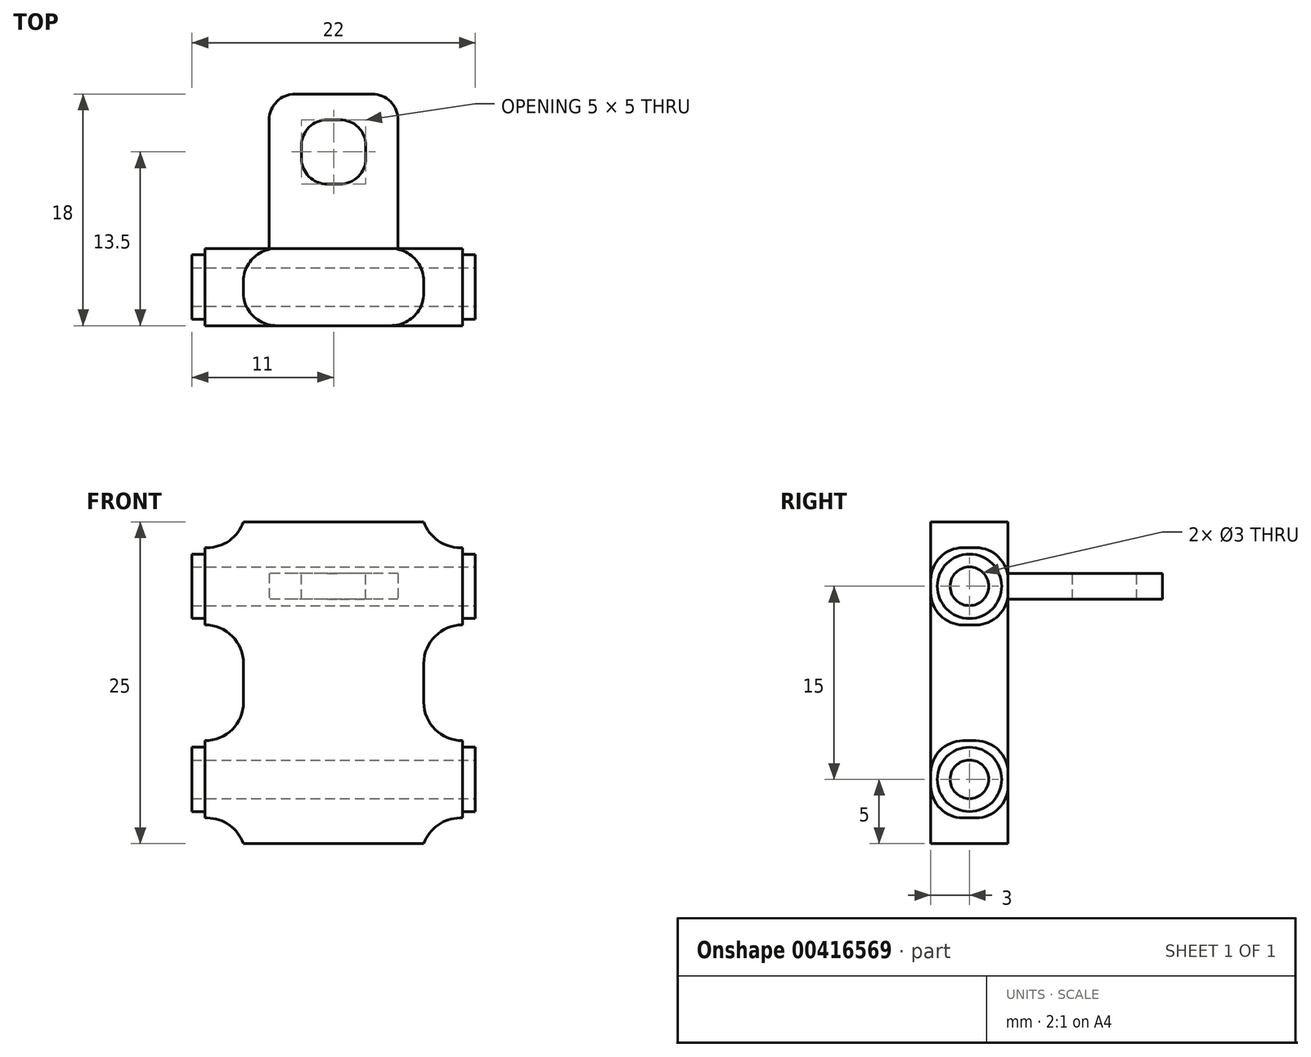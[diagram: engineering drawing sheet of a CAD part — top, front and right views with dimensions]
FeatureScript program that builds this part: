
annotation { "Feature Type Name" : "Feature", "Feature Type Description" : "" }
export const myFeature = defineFeature(function(context is Context, id is Id, definition is map)
    precondition{}
    {
        {
            var Q0;
            Q0=qCreatedBy(makeId("Top.planeOp"),FACE);
            var sketch = newSketch(context, id + "F0", { "sketchPlane" : qUnion([Q0])});
            skLineSegment(sketch, "E0.bottom", {"start": v(-10, 3) * mm, "end": v(10, 3) * mm});
            skLineSegment(sketch, "E0.top", {"start": v(-10, -3) * mm, "end": v(10, -3) * mm});
            skLineSegment(sketch, "E0.left", {"start": v(-10, 3) * mm, "end": v(-10, -3) * mm});
            skLineSegment(sketch, "E0.right", {"start": v(10, 3) * mm, "end": v(10, -3) * mm});
            skSolve(sketch);
        }
        {
            var Q0;
            Q0=makeQuery(id+"F0.imprint","IMPRINT",FACE,{"disambiguationData":[TD([[makeQuery(id+"F0.imprint","IMPRINT",EDGE,{"derivedFrom":sQuery(id+"F0.wireOp",EDGE,"fq8zQIuJ-jQ8N-2xgu-dbAs-BcYjrlKz9kw7")}),-1.0]])]});
            var Q1;
            Q1=makeQuery(id+"F0.imprint","IMPRINT",FACE,{"disambiguationData":[TD([[makeQuery(id+"F0.imprint","IMPRINT",EDGE,{"derivedFrom":sQuery(id+"F0.wireOp",EDGE,"E0.bottom")}),-1.0]])]});
            extrude(context, id + "F1", {"entities" : qUnion([Q0, Q1]), "depth" : 25 * mm});
        }
        {
            var Q0;
            Q0=makeQuery(id+"F1.opExtrude","SWEPT_FACE",FACE,{"disambiguationData":[OSD([sQuery(id+"F0.wireOp",EDGE,"E0.right")])]});
            var sketch = newSketch(context, id + "F2", { "sketchPlane" : qUnion([Q0])});
            skCircle(sketch, "E1", {"center": v(0, 20) * mm, "radius": 1.5 * mm});
            skCircle(sketch, "E2", {"center": v(0, 5) * mm, "radius": 1.5 * mm});
            skCircle(sketch, "E3", {"center": v(0, 20) * mm, "radius": 2.5 * mm});
            skCircle(sketch, "E4", {"center": v(0, 5) * mm, "radius": 2.5 * mm});
            skSolve(sketch);
        }
        {
            var Q0;
            Q0=makeQuery(id+"F2.imprint","IMPRINT",FACE,{"disambiguationData":[TD([[makeQuery(id+"F2.imprint","IMPRINT",EDGE,{"derivedFrom":sQuery(id+"F2.wireOp",EDGE,"E1")}),1.0]])]});
            var Q1;
            Q1=makeQuery(id+"F2.imprint","IMPRINT",FACE,{"disambiguationData":[TD([[makeQuery(id+"F2.imprint","IMPRINT",EDGE,{"derivedFrom":sQuery(id+"F2.wireOp",EDGE,"E2")}),1.0]])]});
            extrude(context, id + "F3", {"entities" : qUnion([Q0, Q1]), "operationType" : NewBodyOperationType.REMOVE, "oppositeDirection" : true, "depth" : 25 * mm});
        }
        {
            var Q0;
            Q0=makeQuery(id+"F1.opExtrude","SWEPT_FACE",FACE,{"disambiguationData":[OSD([sQuery(id+"F0.wireOp",EDGE,"E0.top")])]});
            var sketch = newSketch(context, id + "F4", { "sketchPlane" : qUnion([Q0])});
            skLineSegment(sketch, "E5.bottom", {"start": v(-10, 0) * mm, "end": v(-7, 0) * mm});
            skLineSegment(sketch, "E5.top", {"start": v(-10, 2) * mm, "end": v(-7, 2) * mm});
            skLineSegment(sketch, "E5.left", {"start": v(-10, 0) * mm, "end": v(-10, 2) * mm});
            skLineSegment(sketch, "E5.right", {"start": v(-7, 0) * mm, "end": v(-7, 2) * mm});
            skLineSegment(sketch, "E6.bottom", {"start": v(-10, 25) * mm, "end": v(-7, 25) * mm});
            skLineSegment(sketch, "E6.top", {"start": v(-10, 23) * mm, "end": v(-7, 23) * mm});
            skLineSegment(sketch, "E6.left", {"start": v(-10, 25) * mm, "end": v(-10, 23) * mm});
            skLineSegment(sketch, "E6.right", {"start": v(-7, 25) * mm, "end": v(-7, 23) * mm});
            skLineSegment(sketch, "E7.bottom", {"start": v(-10, 17) * mm, "end": v(-7, 17) * mm});
            skLineSegment(sketch, "E7.top", {"start": v(-10, 8) * mm, "end": v(-7, 8) * mm});
            skLineSegment(sketch, "E7.left", {"start": v(-10, 17) * mm, "end": v(-10, 8) * mm});
            skLineSegment(sketch, "E7.right", {"start": v(-7, 17) * mm, "end": v(-7, 8) * mm});
            skLineSegment(sketch, "E8.bottom", {"start": v(10, 25) * mm, "end": v(7, 25) * mm});
            skLineSegment(sketch, "E8.top", {"start": v(10, 23) * mm, "end": v(7, 23) * mm});
            skLineSegment(sketch, "E8.left", {"start": v(10, 25) * mm, "end": v(10, 23) * mm});
            skLineSegment(sketch, "E8.right", {"start": v(7, 25) * mm, "end": v(7, 23) * mm});
            skLineSegment(sketch, "E9.bottom", {"start": v(10, 0) * mm, "end": v(7, 0) * mm});
            skLineSegment(sketch, "E9.top", {"start": v(10, 2) * mm, "end": v(7, 2) * mm});
            skLineSegment(sketch, "E9.left", {"start": v(10, 0) * mm, "end": v(10, 2) * mm});
            skLineSegment(sketch, "E9.right", {"start": v(7, 0) * mm, "end": v(7, 2) * mm});
            skLineSegment(sketch, "E10.bottom", {"start": v(10, 8) * mm, "end": v(7, 8) * mm});
            skLineSegment(sketch, "E10.top", {"start": v(10, 17) * mm, "end": v(7, 17) * mm});
            skLineSegment(sketch, "E10.left", {"start": v(10, 8) * mm, "end": v(10, 17) * mm});
            skLineSegment(sketch, "E10.right", {"start": v(7, 8) * mm, "end": v(7, 17) * mm});
            skSolve(sketch);
        }
        {
            var Q0;
            Q0=makeQuery(id+"F4.imprint","IMPRINT",FACE,{"disambiguationData":[TD([[makeQuery(id+"F4.imprint","IMPRINT",EDGE,{"derivedFrom":sQuery(id+"F4.wireOp",EDGE,"xABeM33g-2hT4-JnVJ-ANfQ-r4pL9NOcwkph.bottom")}),1.0]])]});
            var Q1;
            Q1=makeQuery(id+"F4.imprint","IMPRINT",FACE,{"disambiguationData":[TD([[makeQuery(id+"F4.imprint","IMPRINT",EDGE,{"derivedFrom":sQuery(id+"F4.wireOp",EDGE,"E6.bottom")}),-1.0]])]});
            var Q2;
            Q2=makeQuery(id+"F4.imprint","IMPRINT",FACE,{"disambiguationData":[TD([[makeQuery(id+"F4.imprint","IMPRINT",EDGE,{"derivedFrom":sQuery(id+"F4.wireOp",EDGE,"E5.bottom")}),1.0]])]});
            var Q3;
            Q3=makeQuery(id+"F4.imprint","IMPRINT",FACE,{"disambiguationData":[TD([[makeQuery(id+"F4.imprint","IMPRINT",EDGE,{"derivedFrom":sQuery(id+"F4.wireOp",EDGE,"Hjx5ZKNc-yqwa-1sJD-JlUp-eHDL7SW7OXiv.bottom")}),-1.0]])]});
            var Q4;
            Q4=makeQuery(id+"F4.imprint","IMPRINT",FACE,{"disambiguationData":[TD([[makeQuery(id+"F4.imprint","IMPRINT",EDGE,{"derivedFrom":sQuery(id+"F4.wireOp",EDGE,"zsafWoAa-VA67-5S50-KdYK-JgLv0a6bxTrw.bottom")}),1.0]])]});
            var Q5;
            Q5=makeQuery(id+"F4.imprint","IMPRINT",FACE,{"disambiguationData":[TD([[makeQuery(id+"F4.imprint","IMPRINT",EDGE,{"derivedFrom":sQuery(id+"F4.wireOp",EDGE,"E7.bottom")}),-1.0]])]});
            var Q6;
            Q6=makeQuery(id+"F4.imprint","IMPRINT",FACE,{"disambiguationData":[TD([[makeQuery(id+"F4.imprint","IMPRINT",EDGE,{"derivedFrom":sQuery(id+"F4.wireOp",EDGE,"E8.bottom")}),-1.0]])]});
            var Q7;
            Q7=makeQuery(id+"F4.imprint","IMPRINT",FACE,{"disambiguationData":[TD([[makeQuery(id+"F4.imprint","IMPRINT",EDGE,{"derivedFrom":sQuery(id+"F4.wireOp",EDGE,"E10.bottom")}),-1.0]])]});
            var Q8;
            Q8=makeQuery(id+"F4.imprint","IMPRINT",FACE,{"disambiguationData":[TD([[makeQuery(id+"F4.imprint","IMPRINT",EDGE,{"derivedFrom":sQuery(id+"F4.wireOp",EDGE,"E9.bottom")}),1.0]])]});
            extrude(context, id + "F5", {"entities" : qUnion([Q0, Q1, Q2, Q3, Q4, Q5, Q6, Q7, Q8]), "operationType" : NewBodyOperationType.REMOVE, "oppositeDirection" : true, "depth" : 25 * mm});
        }
        {
            var Q0;
            Q0=makeQuery(id+"F5.boolean.opBoolean","COPY",EDGE,{"derivedFrom":makeQuery(id+"F5.opExtrude","SWEPT_EDGE",EDGE,{"disambiguationData":[OSD([sQuery(id+"F4.wireOp",EDGE,"xABeM33g-2hT4-JnVJ-ANfQ-r4pL9NOcwkph.top"),sQuery(id+"F4.wireOp",EDGE,"xABeM33g-2hT4-JnVJ-ANfQ-r4pL9NOcwkph.right")])]})});
            var Q1;
            Q1=makeQuery(id+"F5.boolean.opBoolean","COPY",EDGE,{"derivedFrom":makeQuery(id+"F5.opExtrude","SWEPT_EDGE",EDGE,{"disambiguationData":[OSD([sQuery(id+"F4.wireOp",EDGE,"Hjx5ZKNc-yqwa-1sJD-JlUp-eHDL7SW7OXiv.top"),sQuery(id+"F4.wireOp",EDGE,"Hjx5ZKNc-yqwa-1sJD-JlUp-eHDL7SW7OXiv.right")])]})});
            var Q2;
            Q2=makeQuery(id+"F5.boolean.opBoolean","COPY",EDGE,{"derivedFrom":makeQuery(id+"F5.opExtrude","SWEPT_EDGE",EDGE,{"disambiguationData":[OSD([sQuery(id+"F4.wireOp",EDGE,"E6.top"),sQuery(id+"F4.wireOp",EDGE,"E6.right")])]})});
            var Q3;
            Q3=makeQuery(id+"F5.boolean.opBoolean","COPY",EDGE,{"derivedFrom":makeQuery(id+"F5.opExtrude","SWEPT_EDGE",EDGE,{"disambiguationData":[OSD([sQuery(id+"F4.wireOp",EDGE,"E5.top"),sQuery(id+"F4.wireOp",EDGE,"E5.right")])]})});
            var Q4;
            Q4=makeQuery(id+"F5.boolean.opBoolean","COPY",EDGE,{"derivedFrom":makeQuery(id+"F5.opExtrude","SWEPT_EDGE",EDGE,{"disambiguationData":[OSD([sQuery(id+"F4.wireOp",EDGE,"zsafWoAa-VA67-5S50-KdYK-JgLv0a6bxTrw.bottom"),sQuery(id+"F4.wireOp",EDGE,"zsafWoAa-VA67-5S50-KdYK-JgLv0a6bxTrw.right")])]})});
            var Q5;
            Q5=makeQuery(id+"F5.boolean.opBoolean","COPY",EDGE,{"derivedFrom":makeQuery(id+"F5.opExtrude","SWEPT_EDGE",EDGE,{"disambiguationData":[OSD([sQuery(id+"F4.wireOp",EDGE,"zsafWoAa-VA67-5S50-KdYK-JgLv0a6bxTrw.top"),sQuery(id+"F4.wireOp",EDGE,"zsafWoAa-VA67-5S50-KdYK-JgLv0a6bxTrw.right")])]})});
            var Q6;
            Q6=makeQuery(id+"F5.boolean.opBoolean","COPY",EDGE,{"derivedFrom":makeQuery(id+"F5.opExtrude","SWEPT_EDGE",EDGE,{"disambiguationData":[OSD([sQuery(id+"F4.wireOp",EDGE,"E7.top"),sQuery(id+"F4.wireOp",EDGE,"E7.right")])]})});
            var Q7;
            Q7=makeQuery(id+"F5.boolean.opBoolean","COPY",EDGE,{"derivedFrom":makeQuery(id+"F5.opExtrude","SWEPT_EDGE",EDGE,{"disambiguationData":[OSD([sQuery(id+"F4.wireOp",EDGE,"E7.bottom"),sQuery(id+"F4.wireOp",EDGE,"E7.right")])]})});
            var Q8;
            Q8=makeQuery(id+"F5.boolean.opBoolean","COPY",EDGE,{"derivedFrom":makeQuery(id+"F5.opExtrude","SWEPT_EDGE",EDGE,{"disambiguationData":[OSD([sQuery(id+"F4.wireOp",EDGE,"E8.top"),sQuery(id+"F4.wireOp",EDGE,"E8.right")])]})});
            var Q9;
            Q9=makeQuery(id+"F5.boolean.opBoolean","COPY",EDGE,{"derivedFrom":makeQuery(id+"F5.opExtrude","SWEPT_EDGE",EDGE,{"disambiguationData":[OSD([sQuery(id+"F4.wireOp",EDGE,"E10.bottom"),sQuery(id+"F4.wireOp",EDGE,"E10.right")])]})});
            var Q10;
            Q10=makeQuery(id+"F5.boolean.opBoolean","COPY",EDGE,{"derivedFrom":makeQuery(id+"F5.opExtrude","SWEPT_EDGE",EDGE,{"disambiguationData":[OSD([sQuery(id+"F4.wireOp",EDGE,"E10.top"),sQuery(id+"F4.wireOp",EDGE,"E10.right")])]})});
            var Q11;
            Q11=makeQuery(id+"F5.boolean.opBoolean","COPY",EDGE,{"derivedFrom":makeQuery(id+"F5.opExtrude","SWEPT_EDGE",EDGE,{"disambiguationData":[OSD([sQuery(id+"F4.wireOp",EDGE,"E9.top"),sQuery(id+"F4.wireOp",EDGE,"E9.right")])]})});
            fillet(context, id + "F6", {"entities" : qUnion([Q0, Q1, Q2, Q3, Q4, Q5, Q6, Q7, Q8, Q9, Q10, Q11]), "radius" : 3 * mm, "tangentPropagation" : true, "allowEdgeOverflow" : false});
        }
        {
            var Q0;
            Q0=makeQuery(id+"F1.opExtrude","SWEPT_FACE",FACE,{"disambiguationData":[OSD([sQuery(id+"F0.wireOp",EDGE,"E0.bottom")])]});
            var sketch = newSketch(context, id + "F7", { "sketchPlane" : qUnion([Q0])});
            skLineSegment(sketch, "E11.bottom", {"start": v(-5, 21) * mm, "end": v(5, 21) * mm});
            skLineSegment(sketch, "E11.top", {"start": v(-5, 19) * mm, "end": v(5, 19) * mm});
            skLineSegment(sketch, "E11.left", {"start": v(-5, 21) * mm, "end": v(-5, 19) * mm});
            skLineSegment(sketch, "E11.right", {"start": v(5, 21) * mm, "end": v(5, 19) * mm});
            skSolve(sketch);
        }
        {
            var Q0;
            Q0=makeQuery(id+"F7.imprint","IMPRINT",FACE,{"disambiguationData":[TD([[makeQuery(id+"F7.imprint","IMPRINT",EDGE,{"derivedFrom":sQuery(id+"F7.wireOp",EDGE,"E11.bottom")}),-1.0]])]});
            extrude(context, id + "F8", {"entities" : qUnion([Q0]), "operationType" : NewBodyOperationType.ADD, "depth" : 12 * mm});
        }
        {
            var Q0;
            Q0=makeQuery(id+"F8.opExtrude","SWEPT_FACE",FACE,{"disambiguationData":[OSD([sQuery(id+"F7.wireOp",EDGE,"E11.bottom")])]});
            var sketch = newSketch(context, id + "F9", { "sketchPlane" : qUnion([Q0])});
            skLineSegment(sketch, "E12.bottom", {"start": v(-2.5, 13) * mm, "end": v(2.5, 13) * mm});
            skLineSegment(sketch, "E12.top", {"start": v(-2.5, 8) * mm, "end": v(2.5, 8) * mm});
            skLineSegment(sketch, "E12.left", {"start": v(-2.5, 13) * mm, "end": v(-2.5, 8) * mm});
            skLineSegment(sketch, "E12.right", {"start": v(2.5, 13) * mm, "end": v(2.5, 8) * mm});
            skSolve(sketch);
        }
        {
            var Q0;
            Q0=makeQuery(id+"F8.opExtrude","CAP_EDGE",EDGE,{"disambiguationData":[OSD([sQuery(id+"F7.wireOp",EDGE,"E11.right")])],"isStart":false});
            var Q1;
            Q1=makeQuery(id+"F8.opExtrude","CAP_EDGE",EDGE,{"disambiguationData":[OSD([sQuery(id+"F7.wireOp",EDGE,"E11.left")])],"isStart":false});
            var Q2;
            Q2=makeQuery(id+"FuOjLDga9HD541t_1.boolean.opBoolean","COPY",EDGE,{"derivedFrom":makeQuery(id+"FuOjLDga9HD541t_1.opExtrude","SWEPT_EDGE",EDGE,{"disambiguationData":[OSD([sQuery(id+"F9.wireOp",EDGE,"SwnldQ3S-ixUz-o9NJ-gp7F-8rH46QTpGgwd.top"),sQuery(id+"F9.wireOp",EDGE,"SwnldQ3S-ixUz-o9NJ-gp7F-8rH46QTpGgwd.left")])]})});
            var Q3;
            Q3=makeQuery(id+"FuOjLDga9HD541t_1.boolean.opBoolean","COPY",EDGE,{"derivedFrom":makeQuery(id+"FuOjLDga9HD541t_1.opExtrude","SWEPT_EDGE",EDGE,{"disambiguationData":[OSD([sQuery(id+"F9.wireOp",EDGE,"SwnldQ3S-ixUz-o9NJ-gp7F-8rH46QTpGgwd.top"),sQuery(id+"F9.wireOp",EDGE,"SwnldQ3S-ixUz-o9NJ-gp7F-8rH46QTpGgwd.right")])]})});
            fillet(context, id + "F10", {"entities" : qUnion([Q0, Q1, Q2, Q3]), "radius" : 2 * mm, "tangentPropagation" : true, "allowEdgeOverflow" : false});
        }
        {
            var Q0;
            Q0=makeQuery(id+"F2.imprint","IMPRINT",FACE,{"disambiguationData":[TD([[makeQuery(id+"F2.imprint","IMPRINT",EDGE,{"derivedFrom":sQuery(id+"F2.wireOp",EDGE,"E1")}),-1.0]])]});
            var Q1;
            Q1=makeQuery(id+"F2.imprint","IMPRINT",FACE,{"disambiguationData":[TD([[makeQuery(id+"F2.imprint","IMPRINT",EDGE,{"derivedFrom":sQuery(id+"F2.wireOp",EDGE,"E2")}),-1.0]])]});
            extrude(context, id + "F11", {"entities" : qUnion([Q0, Q1]), "operationType" : NewBodyOperationType.ADD, "depth" : 1 * mm});
        }
        {
            var Q0;
            Q0=makeQuery(id+"F5.boolean.opBoolean","SPLIT",FACE,{"disambiguationData":[TD([makeQuery(id+"F3.boolean.opBoolean","COPY",FACE,{"derivedFrom":makeQuery(id+"F3.opExtrude","SWEPT_FACE",FACE,{"disambiguationData":[OSD([sQuery(id+"F2.wireOp",EDGE,"E1")])]})})])],"derivedFrom":makeQuery(id+"F1.opExtrude","SWEPT_FACE",FACE,{"disambiguationData":[OSD([sQuery(id+"F0.wireOp",EDGE,"E0.left")])]})});
            var sketch = newSketch(context, id + "F12", { "sketchPlane" : qUnion([Q0])});
            skCircle(sketch, "E13", {"center": v(0, 20) * mm, "radius": 2.5 * mm});
            skSolve(sketch);
        }
        {
            var Q0;
            Q0=makeQuery(id+"F5.boolean.opBoolean","SPLIT",FACE,{"disambiguationData":[TD([makeQuery(id+"F3.boolean.opBoolean","COPY",FACE,{"derivedFrom":makeQuery(id+"F3.opExtrude","SWEPT_FACE",FACE,{"disambiguationData":[OSD([sQuery(id+"F2.wireOp",EDGE,"E2")])]})})])],"derivedFrom":makeQuery(id+"F1.opExtrude","SWEPT_FACE",FACE,{"disambiguationData":[OSD([sQuery(id+"F0.wireOp",EDGE,"E0.left")])]})});
            var sketch = newSketch(context, id + "F13", { "sketchPlane" : qUnion([Q0])});
            skCircle(sketch, "E14", {"center": v(0, 5) * mm, "radius": 2.5 * mm});
            skSolve(sketch);
        }
        {
            var Q0;
            {var subQ5=sQuery(id+"F0.wireOp",EDGE,"E0.left");var subQ6=makeQuery(id+"F1.opExtrude","SWEPT_FACE",FACE,{"disambiguationData":[OSD([subQ5])]});var subQ10=makeQuery(id+"F3.opExtrude","SWEPT_FACE",FACE,{"disambiguationData":[OSD([sQuery(id+"F2.wireOp",EDGE,"E1")])]});Q0=makeQuery(id+"F12.imprint","IMPRINT",FACE,{"disambiguationData":[TD([[makeQuery(id+"F12.imprint","IMPRINT",EDGE,{"derivedFrom":makeQuery(id+"F3.boolean.opBoolean","INTERSECT",EDGE,{"derivedFrom":[subQ6,subQ10]})}),1.0]])]});}
            var Q1;
            {var subQ3=sQuery(id+"F0.wireOp",EDGE,"E0.left");var subQ4=makeQuery(id+"F1.opExtrude","SWEPT_FACE",FACE,{"disambiguationData":[OSD([subQ3])]});var subQ10=makeQuery(id+"F3.opExtrude","SWEPT_FACE",FACE,{"disambiguationData":[OSD([sQuery(id+"F2.wireOp",EDGE,"E2")])]});Q1=makeQuery(id+"F13.imprint","IMPRINT",FACE,{"disambiguationData":[TD([[makeQuery(id+"F13.imprint","IMPRINT",EDGE,{"derivedFrom":makeQuery(id+"F3.boolean.opBoolean","INTERSECT",EDGE,{"derivedFrom":[subQ4,subQ10]})}),1.0]])]});}
            extrude(context, id + "F14", {"entities" : qUnion([Q0, Q1]), "operationType" : NewBodyOperationType.ADD, "depth" : 1 * mm});
        }
        {
            var Q0;
            Q0=makeQuery(id+"F6.opFillet","BLEND_EDGE",EDGE,{"blendedFrom":[makeQuery(id+"F5.boolean.opBoolean","COPY",EDGE,{"derivedFrom":makeQuery(id+"F5.opExtrude","SWEPT_EDGE",EDGE,{"disambiguationData":[OSD([sQuery(id+"F4.wireOp",EDGE,"E8.top"),sQuery(id+"F4.wireOp",EDGE,"E8.right")])]})}),makeQuery(id+"F1.opExtrude","SWEPT_FACE",FACE,{"disambiguationData":[OSD([sQuery(id+"F0.wireOp",EDGE,"E0.top")])]})],"blendedInto":[makeQuery(id+"F1.opExtrude","SWEPT_FACE",FACE,{"disambiguationData":[OSD([sQuery(id+"F0.wireOp",EDGE,"E0.top")])]})]});
            var Q1;
            Q1=makeQuery(id+"F6.opFillet","BLEND_EDGE",EDGE,{"blendedFrom":[makeQuery(id+"F5.boolean.opBoolean","COPY",EDGE,{"derivedFrom":makeQuery(id+"F5.opExtrude","SWEPT_EDGE",EDGE,{"disambiguationData":[OSD([sQuery(id+"F4.wireOp",EDGE,"E10.bottom"),sQuery(id+"F4.wireOp",EDGE,"E10.right")])]})}),makeQuery(id+"F1.opExtrude","SWEPT_FACE",FACE,{"disambiguationData":[OSD([sQuery(id+"F0.wireOp",EDGE,"E0.top")])]})],"blendedInto":[makeQuery(id+"F1.opExtrude","SWEPT_FACE",FACE,{"disambiguationData":[OSD([sQuery(id+"F0.wireOp",EDGE,"E0.top")])]})]});
            var Q2;
            Q2=makeQuery(id+"F6.opFillet","BLEND_EDGE",EDGE,{"blendedFrom":[makeQuery(id+"F5.boolean.opBoolean","COPY",EDGE,{"derivedFrom":makeQuery(id+"F5.opExtrude","SWEPT_EDGE",EDGE,{"disambiguationData":[OSD([sQuery(id+"F4.wireOp",EDGE,"E10.bottom"),sQuery(id+"F4.wireOp",EDGE,"E10.right")])]})}),makeQuery(id+"F1.opExtrude","SWEPT_FACE",FACE,{"disambiguationData":[OSD([sQuery(id+"F0.wireOp",EDGE,"E0.bottom")])]})],"blendedInto":[makeQuery(id+"F1.opExtrude","SWEPT_FACE",FACE,{"disambiguationData":[OSD([sQuery(id+"F0.wireOp",EDGE,"E0.bottom")])]})]});
            var Q3;
            Q3=makeQuery(id+"F6.opFillet","BLEND_EDGE",EDGE,{"blendedFrom":[makeQuery(id+"F5.boolean.opBoolean","COPY",EDGE,{"derivedFrom":makeQuery(id+"F5.opExtrude","SWEPT_EDGE",EDGE,{"disambiguationData":[OSD([sQuery(id+"F4.wireOp",EDGE,"E9.top"),sQuery(id+"F4.wireOp",EDGE,"E9.right")])]})}),makeQuery(id+"F1.opExtrude","SWEPT_FACE",FACE,{"disambiguationData":[OSD([sQuery(id+"F0.wireOp",EDGE,"E0.bottom")])]})],"blendedInto":[makeQuery(id+"F1.opExtrude","SWEPT_FACE",FACE,{"disambiguationData":[OSD([sQuery(id+"F0.wireOp",EDGE,"E0.bottom")])]})]});
            var Q4;
            Q4=makeQuery(id+"F6.opFillet","BLEND_EDGE",EDGE,{"blendedFrom":[makeQuery(id+"F5.boolean.opBoolean","COPY",EDGE,{"derivedFrom":makeQuery(id+"F5.opExtrude","SWEPT_EDGE",EDGE,{"disambiguationData":[OSD([sQuery(id+"F4.wireOp",EDGE,"E9.top"),sQuery(id+"F4.wireOp",EDGE,"E9.right")])]})}),makeQuery(id+"F1.opExtrude","SWEPT_FACE",FACE,{"disambiguationData":[OSD([sQuery(id+"F0.wireOp",EDGE,"E0.top")])]})],"blendedInto":[makeQuery(id+"F1.opExtrude","SWEPT_FACE",FACE,{"disambiguationData":[OSD([sQuery(id+"F0.wireOp",EDGE,"E0.top")])]})]});
            var Q5;
            Q5=makeQuery(id+"F6.opFillet","BLEND_EDGE",EDGE,{"blendedFrom":[makeQuery(id+"F5.boolean.opBoolean","COPY",EDGE,{"derivedFrom":makeQuery(id+"F5.opExtrude","SWEPT_EDGE",EDGE,{"disambiguationData":[OSD([sQuery(id+"F4.wireOp",EDGE,"E5.top"),sQuery(id+"F4.wireOp",EDGE,"E5.right")])]})}),makeQuery(id+"F1.opExtrude","SWEPT_FACE",FACE,{"disambiguationData":[OSD([sQuery(id+"F0.wireOp",EDGE,"E0.bottom")])]})],"blendedInto":[makeQuery(id+"F1.opExtrude","SWEPT_FACE",FACE,{"disambiguationData":[OSD([sQuery(id+"F0.wireOp",EDGE,"E0.bottom")])]})]});
            var Q6;
            Q6=makeQuery(id+"F6.opFillet","BLEND_EDGE",EDGE,{"blendedFrom":[makeQuery(id+"F5.boolean.opBoolean","COPY",EDGE,{"derivedFrom":makeQuery(id+"F5.opExtrude","SWEPT_EDGE",EDGE,{"disambiguationData":[OSD([sQuery(id+"F4.wireOp",EDGE,"E7.bottom"),sQuery(id+"F4.wireOp",EDGE,"E7.right")])]})}),makeQuery(id+"F1.opExtrude","SWEPT_FACE",FACE,{"disambiguationData":[OSD([sQuery(id+"F0.wireOp",EDGE,"E0.bottom")])]})],"blendedInto":[makeQuery(id+"F1.opExtrude","SWEPT_FACE",FACE,{"disambiguationData":[OSD([sQuery(id+"F0.wireOp",EDGE,"E0.bottom")])]})]});
            var Q7;
            Q7=makeQuery(id+"F6.opFillet","BLEND_EDGE",EDGE,{"blendedFrom":[makeQuery(id+"F5.boolean.opBoolean","COPY",EDGE,{"derivedFrom":makeQuery(id+"F5.opExtrude","SWEPT_EDGE",EDGE,{"disambiguationData":[OSD([sQuery(id+"F4.wireOp",EDGE,"E7.bottom"),sQuery(id+"F4.wireOp",EDGE,"E7.right")])]})}),makeQuery(id+"F1.opExtrude","SWEPT_FACE",FACE,{"disambiguationData":[OSD([sQuery(id+"F0.wireOp",EDGE,"E0.top")])]})],"blendedInto":[makeQuery(id+"F1.opExtrude","SWEPT_FACE",FACE,{"disambiguationData":[OSD([sQuery(id+"F0.wireOp",EDGE,"E0.top")])]})]});
            var Q8;
            Q8=makeQuery(id+"F6.opFillet","BLEND_EDGE",EDGE,{"blendedFrom":[makeQuery(id+"F5.boolean.opBoolean","COPY",EDGE,{"derivedFrom":makeQuery(id+"F5.opExtrude","SWEPT_EDGE",EDGE,{"disambiguationData":[OSD([sQuery(id+"F4.wireOp",EDGE,"E6.top"),sQuery(id+"F4.wireOp",EDGE,"E6.right")])]})}),makeQuery(id+"F1.opExtrude","SWEPT_FACE",FACE,{"disambiguationData":[OSD([sQuery(id+"F0.wireOp",EDGE,"E0.top")])]})],"blendedInto":[makeQuery(id+"F1.opExtrude","SWEPT_FACE",FACE,{"disambiguationData":[OSD([sQuery(id+"F0.wireOp",EDGE,"E0.top")])]})]});
            var Q9;
            Q9=makeQuery(id+"F6.opFillet","BLEND_EDGE",EDGE,{"blendedFrom":[makeQuery(id+"F5.boolean.opBoolean","COPY",EDGE,{"derivedFrom":makeQuery(id+"F5.opExtrude","SWEPT_EDGE",EDGE,{"disambiguationData":[OSD([sQuery(id+"F4.wireOp",EDGE,"E6.top"),sQuery(id+"F4.wireOp",EDGE,"E6.right")])]})}),makeQuery(id+"F1.opExtrude","SWEPT_FACE",FACE,{"disambiguationData":[OSD([sQuery(id+"F0.wireOp",EDGE,"E0.bottom")])]})],"blendedInto":[makeQuery(id+"F1.opExtrude","SWEPT_FACE",FACE,{"disambiguationData":[OSD([sQuery(id+"F0.wireOp",EDGE,"E0.bottom")])]})]});
            var Q10;
            Q10=makeQuery(id+"F6.opFillet","BLEND_EDGE",EDGE,{"blendedFrom":[makeQuery(id+"F5.boolean.opBoolean","COPY",EDGE,{"derivedFrom":makeQuery(id+"F5.opExtrude","SWEPT_EDGE",EDGE,{"disambiguationData":[OSD([sQuery(id+"F4.wireOp",EDGE,"E8.top"),sQuery(id+"F4.wireOp",EDGE,"E8.right")])]})}),makeQuery(id+"F1.opExtrude","SWEPT_FACE",FACE,{"disambiguationData":[OSD([sQuery(id+"F0.wireOp",EDGE,"E0.bottom")])]})],"blendedInto":[makeQuery(id+"F1.opExtrude","SWEPT_FACE",FACE,{"disambiguationData":[OSD([sQuery(id+"F0.wireOp",EDGE,"E0.bottom")])]})]});
            var Q11;
            Q11=makeQuery(id+"F6.opFillet","BLEND_EDGE",EDGE,{"blendedFrom":[makeQuery(id+"F5.boolean.opBoolean","COPY",EDGE,{"derivedFrom":makeQuery(id+"F5.opExtrude","SWEPT_EDGE",EDGE,{"disambiguationData":[OSD([sQuery(id+"F4.wireOp",EDGE,"E5.top"),sQuery(id+"F4.wireOp",EDGE,"E5.right")])]})}),makeQuery(id+"F1.opExtrude","SWEPT_FACE",FACE,{"disambiguationData":[OSD([sQuery(id+"F0.wireOp",EDGE,"E0.top")])]})],"blendedInto":[makeQuery(id+"F1.opExtrude","SWEPT_FACE",FACE,{"disambiguationData":[OSD([sQuery(id+"F0.wireOp",EDGE,"E0.top")])]})]});
            fillet(context, id + "F15", {"entities" : qUnion([Q0, Q1, Q2, Q3, Q4, Q5, Q6, Q7, Q8, Q9, Q10, Q11]), "radius" : 2.5 * mm, "tangentPropagation" : true, "allowEdgeOverflow" : false});
        }
        {
            var Q0;
            Q0=makeQuery(id+"F9.imprint","IMPRINT",FACE,{"disambiguationData":[TD([[makeQuery(id+"F9.imprint","IMPRINT",EDGE,{"derivedFrom":sQuery(id+"F9.wireOp",EDGE,"E12.bottom")}),-1.0]])]});
            extrude(context, id + "F16", {"entities" : qUnion([Q0]), "operationType" : NewBodyOperationType.REMOVE, "oppositeDirection" : true, "depth" : 25 * mm});
        }
        {
            var Q0;
            Q0=makeQuery(id+"F16.boolean.opBoolean","COPY",EDGE,{"derivedFrom":makeQuery(id+"F16.opExtrude","SWEPT_EDGE",EDGE,{"disambiguationData":[OSD([sQuery(id+"F9.wireOp",EDGE,"E12.bottom"),sQuery(id+"F9.wireOp",EDGE,"E12.left")])]})});
            var Q1;
            Q1=makeQuery(id+"F16.boolean.opBoolean","COPY",EDGE,{"derivedFrom":makeQuery(id+"F16.opExtrude","SWEPT_EDGE",EDGE,{"disambiguationData":[OSD([sQuery(id+"F9.wireOp",EDGE,"E12.top"),sQuery(id+"F9.wireOp",EDGE,"E12.left")])]})});
            var Q2;
            Q2=makeQuery(id+"F16.boolean.opBoolean","COPY",EDGE,{"derivedFrom":makeQuery(id+"F16.opExtrude","SWEPT_EDGE",EDGE,{"disambiguationData":[OSD([sQuery(id+"F9.wireOp",EDGE,"E12.top"),sQuery(id+"F9.wireOp",EDGE,"E12.right")])]})});
            var Q3;
            Q3=makeQuery(id+"F16.boolean.opBoolean","COPY",EDGE,{"derivedFrom":makeQuery(id+"F16.opExtrude","SWEPT_EDGE",EDGE,{"disambiguationData":[OSD([sQuery(id+"F9.wireOp",EDGE,"E12.bottom"),sQuery(id+"F9.wireOp",EDGE,"E12.right")])]})});
            fillet(context, id + "F17", {"entities" : qUnion([Q0, Q1, Q2, Q3]), "radius" : 2 * mm, "tangentPropagation" : true, "allowEdgeOverflow" : false});
        }
    });
